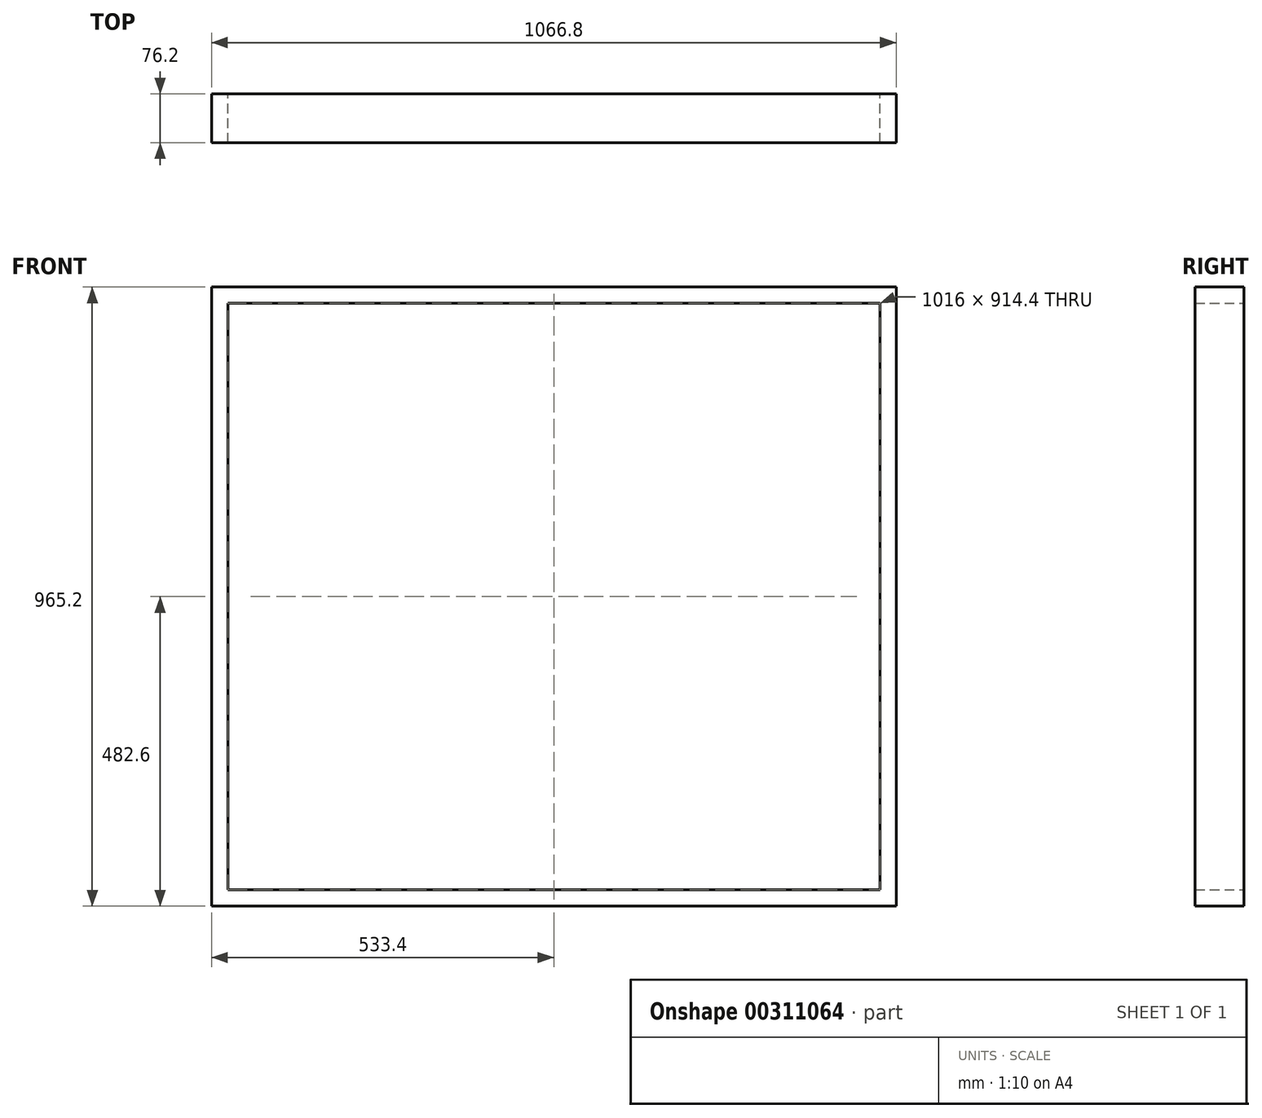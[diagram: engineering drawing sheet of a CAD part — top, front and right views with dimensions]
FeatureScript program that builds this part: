
annotation { "Feature Type Name" : "Feature", "Feature Type Description" : "" }
export const myFeature = defineFeature(function(context is Context, id is Id, definition is map)
    precondition{}
    {
        {
            var Q0;
            Q0=qCreatedBy(makeId("Front.planeOp"),FACE);
            var sketch = newSketch(context, id + "F0", { "sketchPlane" : qUnion([Q0])});
            skLineSegment(sketch, "E0.bottom", {"start": v(0, 0) * mm, "end": v(1066.8, 0) * mm});
            skLineSegment(sketch, "E0.top", {"start": v(0, 965.2) * mm, "end": v(1066.8, 965.2) * mm});
            skLineSegment(sketch, "E0.left", {"start": v(0, 0) * mm, "end": v(0, 965.2) * mm});
            skLineSegment(sketch, "E0.right", {"start": v(1066.8, 0) * mm, "end": v(1066.8, 965.2) * mm});
            skLineSegment(sketch, "E1.0", {"start": v(25.4, 939.8) * mm, "end": v(1041.4, 939.8) * mm});
            skLineSegment(sketch, "E1.1", {"start": v(25.4, 25.4) * mm, "end": v(25.4, 939.8) * mm});
            skLineSegment(sketch, "E1.2", {"start": v(25.4, 25.4) * mm, "end": v(1041.4, 25.4) * mm});
            skLineSegment(sketch, "E1.3", {"start": v(1041.4, 25.4) * mm, "end": v(1041.4, 939.8) * mm});
            skSolve(sketch);
        }
        {
            var Q0;
            Q0=makeQuery(id+"F0.imprint","IMPRINT",FACE,{"disambiguationData":[TD([[makeQuery(id+"F0.imprint","IMPRINT",EDGE,{"derivedFrom":sQuery(id+"F0.wireOp",EDGE,"E0.bottom")}),1.0]])]});
            extrude(context, id + "F1", {"entities" : qUnion([Q0]), "depth" : 76.2 * mm});
        }
    });
